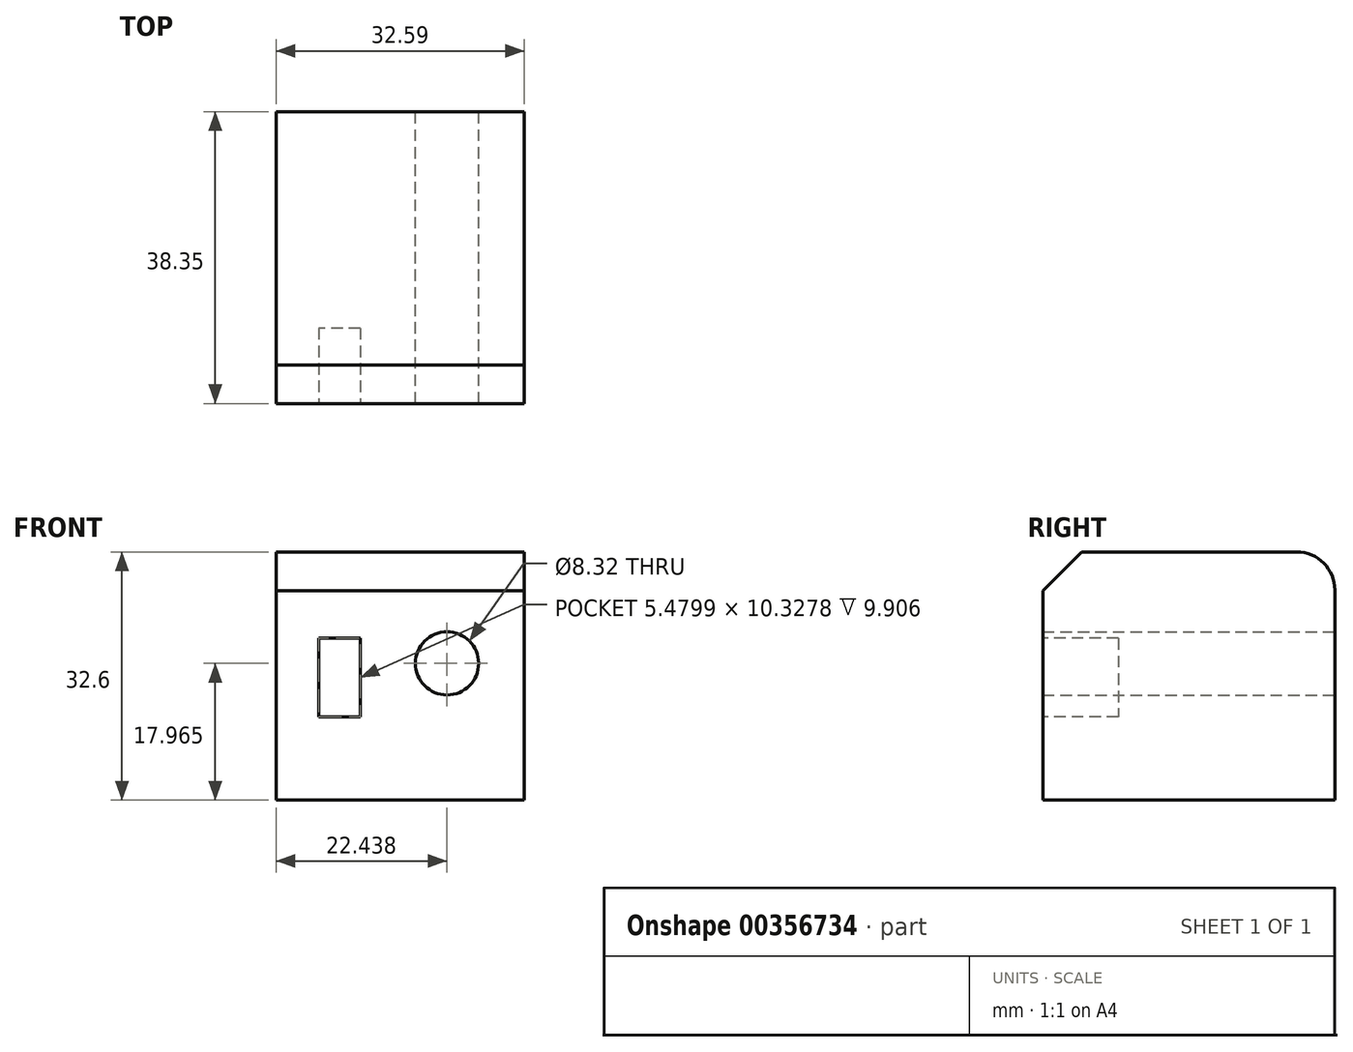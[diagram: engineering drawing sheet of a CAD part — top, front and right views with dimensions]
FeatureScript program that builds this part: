
annotation { "Feature Type Name" : "Feature", "Feature Type Description" : "" }
export const myFeature = defineFeature(function(context is Context, id is Id, definition is map)
    precondition{}
    {
        {
            var Q0;
            Q0=qCreatedBy(makeId("Front.planeOp"),FACE);
            var sketch = newSketch(context, id + "F0", { "sketchPlane" : qUnion([Q0])});
            skLineSegment(sketch, "E0.bottom", {"start": v(-66.65, 61.8) * mm, "end": v(-34.06, 61.8) * mm});
            skLineSegment(sketch, "E0.top", {"start": v(-66.65, 29.21) * mm, "end": v(-34.06, 29.21) * mm});
            skLineSegment(sketch, "E0.left", {"start": v(-66.65, 61.8) * mm, "end": v(-66.65, 29.21) * mm});
            skLineSegment(sketch, "E0.right", {"start": v(-34.06, 61.8) * mm, "end": v(-34.06, 29.21) * mm});
            skSolve(sketch);
        }
        {
            var Q0;
            Q0=makeQuery(id+"F0.imprint","IMPRINT",FACE,{"disambiguationData":[TD([[makeQuery(id+"F0.imprint","IMPRINT",EDGE,{"derivedFrom":sQuery(id+"F0.wireOp",EDGE,"E0.bottom")}),-1.0]])]});
            extrude(context, id + "F1", {"entities" : qUnion([Q0]), "depth" : 38.35 * mm});
        }
        {
            var Q0;
            Q0=makeQuery(id+"F1.opExtrude","CAP_EDGE",EDGE,{"disambiguationData":[OSD([sQuery(id+"F0.wireOp",EDGE,"E0.bottom")])],"isStart":false});
            chamfer(context, id + "F2", {"entities" : qUnion([Q0]), "width" : 5.08 * mm, "tangentPropagation" : true});
        }
        {
            var Q0;
            Q0=makeQuery(id+"F0.imprint","IMPRINT",FACE,{"disambiguationData":[TD([[makeQuery(id+"F0.imprint","IMPRINT",EDGE,{"derivedFrom":sQuery(id+"F0.wireOp",EDGE,"E0.bottom")}),-1.0]])]});
            var sketch = newSketch(context, id + "F3", { "sketchPlane" : qUnion([Q0])});
            skCircle(sketch, "E1", {"center": v(-44.21, 47.17) * mm, "radius": 4.16 * mm});
            skSolve(sketch);
        }
        {
            var Q0;
            Q0=makeQuery(id+"F3.imprint","IMPRINT",FACE,{"disambiguationData":[TD([[makeQuery(id+"F3.imprint","IMPRINT",EDGE,{"derivedFrom":sQuery(id+"F3.wireOp",EDGE,"E1")}),1.0]])]});
            extrude(context, id + "F4", {"entities" : qUnion([Q0]), "operationType" : NewBodyOperationType.REMOVE, "depth" : 40.13 * mm});
        }
        {
            var Q0;
            Q0=makeQuery(id+"F1.opExtrude","CAP_FACE",FACE,{"disambiguationData":[OSD([sQuery(id+"F0.wireOp",EDGE,"E0.bottom"),sQuery(id+"F0.wireOp",EDGE,"E0.top"),sQuery(id+"F0.wireOp",EDGE,"E0.left"),sQuery(id+"F0.wireOp",EDGE,"E0.right")])],"isStart":false});
            var sketch = newSketch(context, id + "F5", { "sketchPlane" : qUnion([Q0])});
            skLineSegment(sketch, "E2.bottom", {"start": v(-55.6, 50.46) * mm, "end": v(-61.08, 50.46) * mm});
            skLineSegment(sketch, "E2.top", {"start": v(-55.6, 40.13) * mm, "end": v(-61.08, 40.13) * mm});
            skLineSegment(sketch, "E2.left", {"start": v(-55.6, 50.46) * mm, "end": v(-55.6, 40.13) * mm});
            skLineSegment(sketch, "E2.right", {"start": v(-61.08, 50.46) * mm, "end": v(-61.08, 40.13) * mm});
            skSolve(sketch);
        }
        {
            var Q0;
            Q0=makeQuery(id+"F5.imprint","IMPRINT",FACE,{"disambiguationData":[TD([[makeQuery(id+"F5.imprint","IMPRINT",EDGE,{"derivedFrom":sQuery(id+"F5.wireOp",EDGE,"E2.bottom")}),1.0]])]});
            extrude(context, id + "F6", {"entities" : qUnion([Q0]), "operationType" : NewBodyOperationType.REMOVE, "oppositeDirection" : true, "depth" : 9.9 * mm});
        }
        {
            var Q0;
            Q0=makeQuery(id+"F1.opExtrude","CAP_EDGE",EDGE,{"disambiguationData":[OSD([sQuery(id+"F0.wireOp",EDGE,"E0.bottom")])],"isStart":true});
            fillet(context, id + "F7", {"entities" : qUnion([Q0]), "radius" : 5 * mm, "tangentPropagation" : true, "allowEdgeOverflow" : false});
        }
    });
